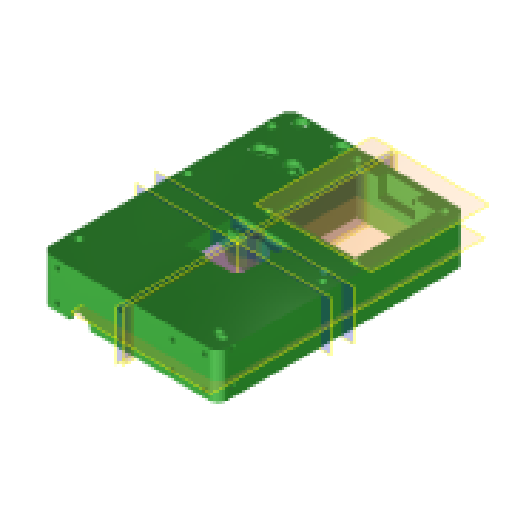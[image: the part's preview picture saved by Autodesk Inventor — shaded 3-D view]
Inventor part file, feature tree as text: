
AUTODESK INVENTOR PART (.ipt)
format: ipt  version: 2024.1 (Build 281209000, 209)  size: 614,400 bytes
history: native  units: mm
features: plane x7, other x6, sketch x4, extrude x1, reference x1, projected_geometry x1
ambient origin geometry x8: Origin, YZ Plane, XZ Plane, XY Plane, X Axis, Y Axis, Z Axis, Center Point
bodies: Volumenkörper1 (feature_tree)
feature tree (20):
  other  "60_Planktoscope_Base_half_wormdrive_1.ipt"
  extrude  "Extrusion1"  Depth=10.0mm TaperAngle=0.0deg
  other  "Volumenkörper1::60_Planktoscope_Base_half_wormdrive_1.ipt"
  other  "Bezeichnung1"
  sketch  "Skizze1"  dims[d0=10.0mm d1=10.0mm d2=0.0mm]
  sketch  "Skizze2"
  sketch  "Skizze17"
  plane  "Arbeitsebene1"
  plane  "Arbeitsebene2"
  plane  "Arbeitsebene3"
  plane  "Arbeitsebene4"
  plane  "Arbeitsebene5"
  plane  "Arbeitsebene6"
  plane  "Arbeitsebene7"
  other  "Arbeitsachse1"
  sketch  "Skizze18"
  reference  "Referenz1"
  projected_geometry  "Projizierte Kontur1"
  other  "Assembly_Planktoscope_Uc2version_wormdrive_V3.iam"
  other  "00_NEMA11:1"
